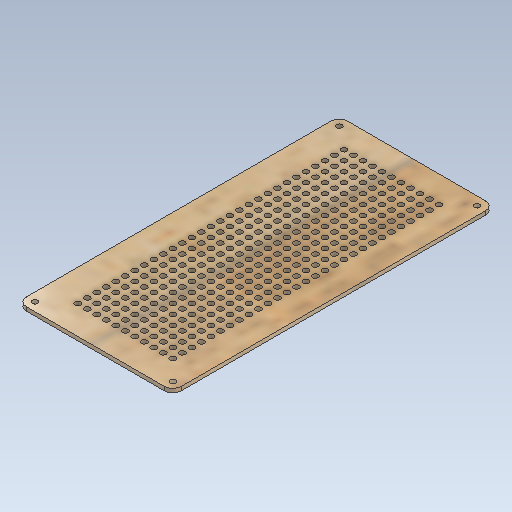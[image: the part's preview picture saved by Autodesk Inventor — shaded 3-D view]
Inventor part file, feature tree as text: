
AUTODESK INVENTOR PART (.ipt)
format: ipt  version: 2020.3 (Build 243373000, 373)  size: 534,016 bytes
history: native  units: mm
features: sketch x2, other x1, extrude x1, hole x1, fillet x1
ambient origin geometry x8: Origin, YZ Plane, XZ Plane, XY Plane, X Axis, Y Axis, Z Axis, Center Point
bodies: Body1 (feature_tree)
feature tree (6):
  other  "ソリッド1"
  extrude  "押し出し1"  Depth=169.0mm
  hole  "穴1"  [1 undecoded]
  fillet  "フィレット1"  Radius=160.0mm
  sketch  "スケッチ1"
  sketch  "スケッチ2"
note: 1 required parameter value undecoded (feature->parameter linkage not recoverable at this tier; creation-order binding heuristic only, values carry confidence <= 0.55)
